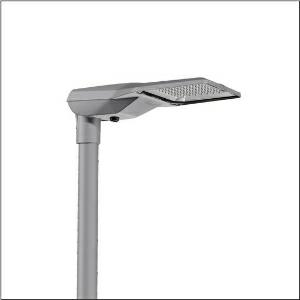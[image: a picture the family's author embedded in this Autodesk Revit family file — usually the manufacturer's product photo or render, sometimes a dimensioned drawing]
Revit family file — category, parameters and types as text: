
# Revit family: streetlight_sl_21_midi___p0_8ab_5xe3r33r08mb_58ac
name_source: partatom
category: Lighting Fixtures
units: mm (PartAtom-declared; Revit-internal decimal feet)

## family parameters
Cut with Voids When Loaded = No
Host = Face
Light Source = No
Part Type = Normal
Room Calculation Point = No
Round Connector Dimension = Use Diameter
Shared = No

## types (1)
- --- (1 x LED, 15870 lm, 136 W, 3000K)
    Apparent Load = 136 VA
    CIE Flux Codes = 36 71 98 100 100
    Color Rendering = 70
    Color Temperature = 3000K
    Default Elevation = 1800 mm
    Description = Streetlight SL 21 midi, mast luminaire, primary light control with lens, of PMMA, primary optical cover: cover, of toughened safety glass, transparent, light distribution: P0.8aB, light emission: direct distribution, primary light characteristic: asymmetric, installation type: post-top, side-entry, LED, High Power LED, rated luminous flux: 15.870lm, luminous efficacy: 117lm/W, light colour: 730, colour temperature: 3000K, control gear: D4i, control: pre-setting: logarithmic dimming characteristic, flexible luminous flux parameterisation, time-dependent luminous flux control, constant luminous flux control, overheat protection, mains connection: 230..240V, AC, 50/60Hz, start of lifetime: 136W, end of service life: 142W, reduction: 61W, luminaire housing, of diecast aluminium, powder-coated, SITECO metallic grey (DB 702S), corrosivity category C5 high according to DIN EN ISO 12944, multi-level sealing system, sealing non-destructively replaceable, inclination adjustable: 0°, 5°, 10°, 15°, please order mast flange separately, length: 644mm, width: 335mm, height: 110mm, mast flange for spigot size: 42mm (side-entry): 5XC10008XM4, 60/48mm (side-entry/post-top): 5XC10108XM2, 76/60mm (side-entry/post-top): 5XC10108XM1, mounting height: 4..8m, Smart Interface below, protection rating (complete): IP66, insulation class (complete): insulation class II (safety insulation), certification: CE, ENEC, ENEC+, VDE, impact resistance: IK10, permissible operating ambient temperature for outdoor applications: -40..+50°C, standard-compliant lighting for roads and squares, packaging unit: 1 piece

Light Distribution: P0.8aB
    Height = 111 mm
    Lamp = 1 x LED
    Lamp Light Flux = 15870 lm
    Lamp Power = 136 W
    Lamp count = 1
    Length = 644 mm
    Luminous efficacy = 117 lm/W
    Manufacturer = Siteco
    ModVariant = No
    Model = 5XE3R33R08MB
    Number of Poles = 1
    OnlyDefault = Yes
    Power Factor = 1
    Product Name = Streetlight SL 21 midi | P0.8aB
    Product group = mast luminaire | pylon top
    ProductGroupID = 6100
    Protection Class = Protection class II
    Protection Degree = IP 66
    RLX_Detail_Level = 1
    RLX_Emergency_Light_Flux = 0 lm
    RLX_Emergency_Type = 0
    RLX_Emergency_Type_DB = No
    RlxData = <blob elided: 90229 chars, md5=4e46696e>
    Socket = socket
    Standby Power = 0 W
    System Light Flux = 15870 lm
    System Power = 136 W
    Type Comments = factory setting: luminous flux: 100 % | dim-lin: 254 | 695 mA
    Type Image = l_1004300.jpg
    URL = http://relux.com
    VarID = @adj_082785
    Voltage = 0 V
    Weight = 0.00 kg
    Width = 336 mm

## geometry (parser evidence)
native form markers: Blend x4, Sweep x12
no freeform markers — native parametric forms only
